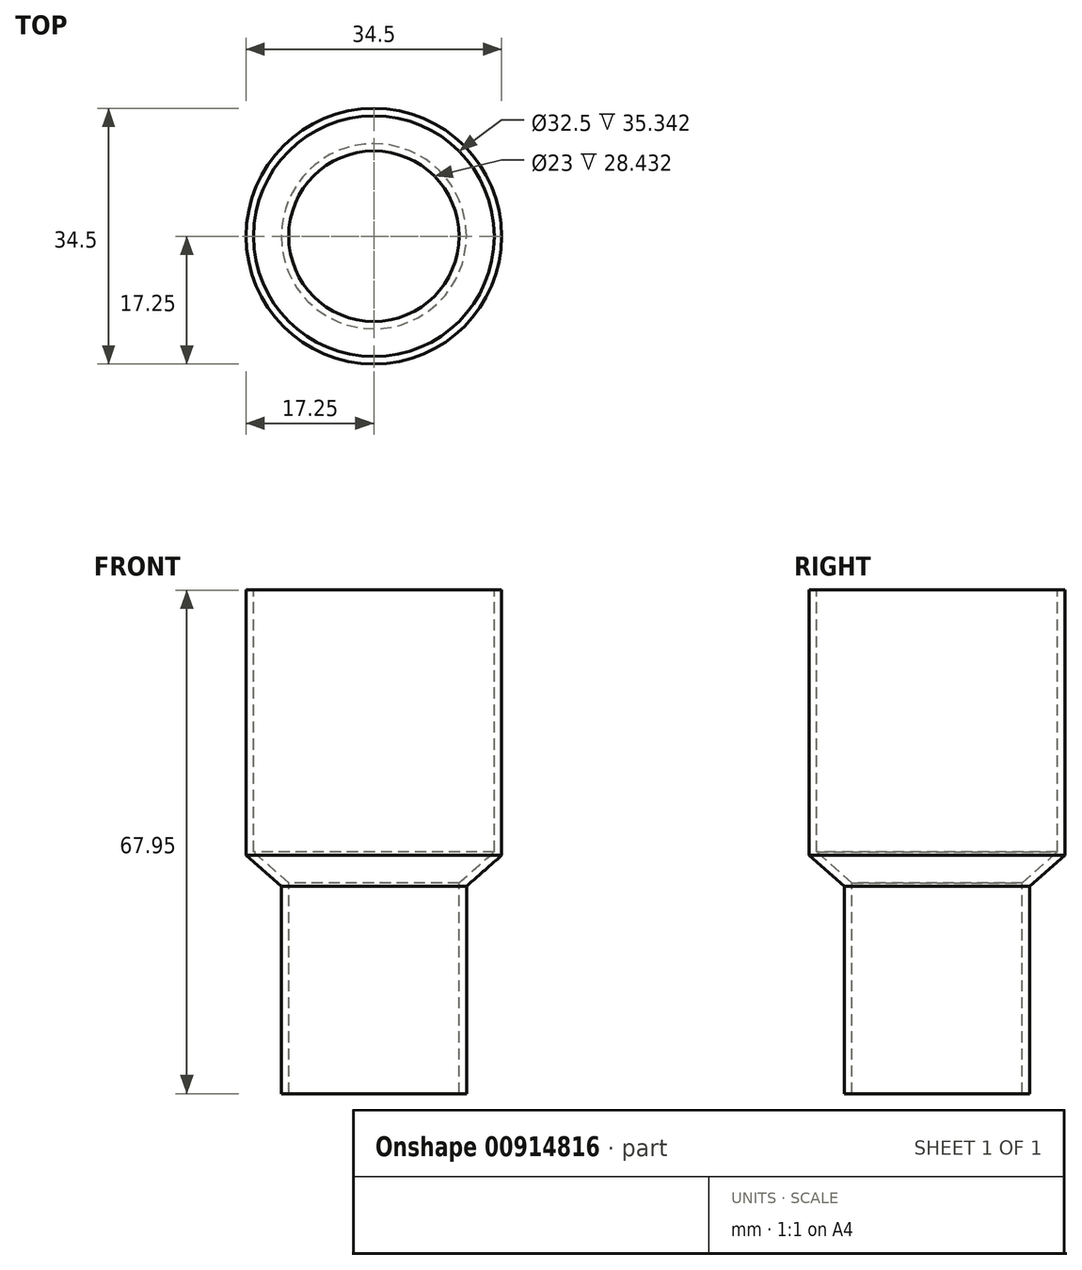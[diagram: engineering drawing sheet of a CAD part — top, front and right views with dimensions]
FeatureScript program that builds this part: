
annotation { "Feature Type Name" : "Feature", "Feature Type Description" : "" }
export const myFeature = defineFeature(function(context is Context, id is Id, definition is map)
    precondition{}
    {
        {
            var Q0;
            Q0=qCreatedBy(makeId("Front.planeOp"),FACE);
            var sketch = newSketch(context, id + "F0", { "sketchPlane" : qUnion([Q0])});
            skLineSegment(sketch, "E0.top", {"start": v(17.25, 35.8) * mm, "end": v(-17.25, 35.8) * mm});
            skLineSegment(sketch, "E0.left", {"start": v(17.25, 0) * mm, "end": v(17.25, 35.8) * mm});
            skLineSegment(sketch, "E0.right", {"start": v(-17.25, 0) * mm, "end": v(-17.25, 35.8) * mm});
            skPoint(sketch, "E0.middle", {"position": v(0, 17.9) * mm});
            skLineSegment(sketch, "E1.top", {"start": v(12.5, -32.16) * mm, "end": v(-12.5, -32.16) * mm});
            skLineSegment(sketch, "E1.left", {"start": v(12.5, -4.18) * mm, "end": v(12.5, -32.16) * mm});
            skLineSegment(sketch, "E1.right", {"start": v(-12.5, -4.18) * mm, "end": v(-12.5, -32.16) * mm});
            skPoint(sketch, "E1.middle", {"position": v(0, -15.23) * mm});
            skLineSegment(sketch, "E2", {"start": v(-17.25, 0) * mm, "end": v(-12.5, -4.18) * mm});
            skLineSegment(sketch, "E3", {"start": v(17.25, 0) * mm, "end": v(12.5, -4.18) * mm});
            skPoint(sketch, "E4.orphan", {"position": v(12.5, 1.7) * mm});
            skPoint(sketch, "E0.bottom.end.orphan", {"position": v(-12.5, 1.7) * mm});
            skLineSegment(sketch, "E5", {"start": v(0, 35.8) * mm, "end": v(0, -32.16) * mm});
            skLineSegment(sketch, "E6", {"start": v(-12.5, -4.18) * mm, "end": v(12.5, -4.18) * mm});
            skLineSegment(sketch, "E7", {"start": v(-17.25, 0) * mm, "end": v(17.25, 0) * mm});
            skSolve(sketch);
        }
        {
            var Q0;
            {var subQ0=sQuery(id+"F0.wireOp",EDGE,"E0.right");Q0=makeQuery(id+"F0.imprint","IMPRINT",FACE,{"disambiguationData":[TD([[makeQuery(id+"F0.imprint","IMPRINT",EDGE,{"derivedFrom":subQ0}),-1.0]])]});}
            var Q1;
            {var subQ0=sQuery(id+"F0.wireOp",EDGE,"E2");Q1=makeQuery(id+"F0.imprint","IMPRINT",FACE,{"disambiguationData":[TD([[makeQuery(id+"F0.imprint","IMPRINT",EDGE,{"derivedFrom":subQ0}),1.0]])]});}
            var Q2;
            {var subQ0=sQuery(id+"F0.wireOp",EDGE,"E1.right");Q2=makeQuery(id+"F0.imprint","IMPRINT",FACE,{"disambiguationData":[TD([[makeQuery(id+"F0.imprint","IMPRINT",EDGE,{"derivedFrom":subQ0}),1.0]])]});}
            var Q3;
            Q3=sQuery(id+"F0.wireOp",EDGE,"E5");
            revolve(context, id + "F1", {"surfaceOperationType" : NewSurfaceOperationType.NEW, "entities" : qUnion([Q0, Q1, Q2]), "axis" : qUnion([Q3]), "revolveType" : RevolveType.FULL});
        }
        {
            var Q0;
            Q0=makeQuery(id+"F1.opRevolve","SWEPT_FACE",FACE,{"disambiguationData":[OSD([sQuery(id+"F0.wireOp",EDGE,"E1.top")])]});
            var sketch = newSketch(context, id + "F2", { "sketchPlane" : qUnion([Q0])});
            skCircle(sketch, "E8", {"center": v(0, 0) * mm, "radius": 11.5 * mm});
            skSolve(sketch);
        }
        {
            var Q0;
            Q0=makeQuery(id+"F1.opRevolve","SWEPT_FACE",FACE,{"disambiguationData":[OSD([sQuery(id+"F0.wireOp",EDGE,"E0.top")])]});
            shell(context, id + "F3", {"entities" : qUnion([Q0]), "thickness" : 1 * mm});
        }
        {
            var Q0;
            Q0=makeQuery(id+"F2.imprint","IMPRINT",FACE,{"disambiguationData":[TD([[makeQuery(id+"F2.imprint","IMPRINT",EDGE,{"derivedFrom":sQuery(id+"F2.wireOp",EDGE,"E8")}),1.0]])]});
            extrude(context, id + "F4", {"entities" : qUnion([Q0]), "operationType" : NewBodyOperationType.REMOVE, "oppositeDirection" : true, "depth" : 40 * mm, "offsetDistance" : 25 * mm});
        }
    });
